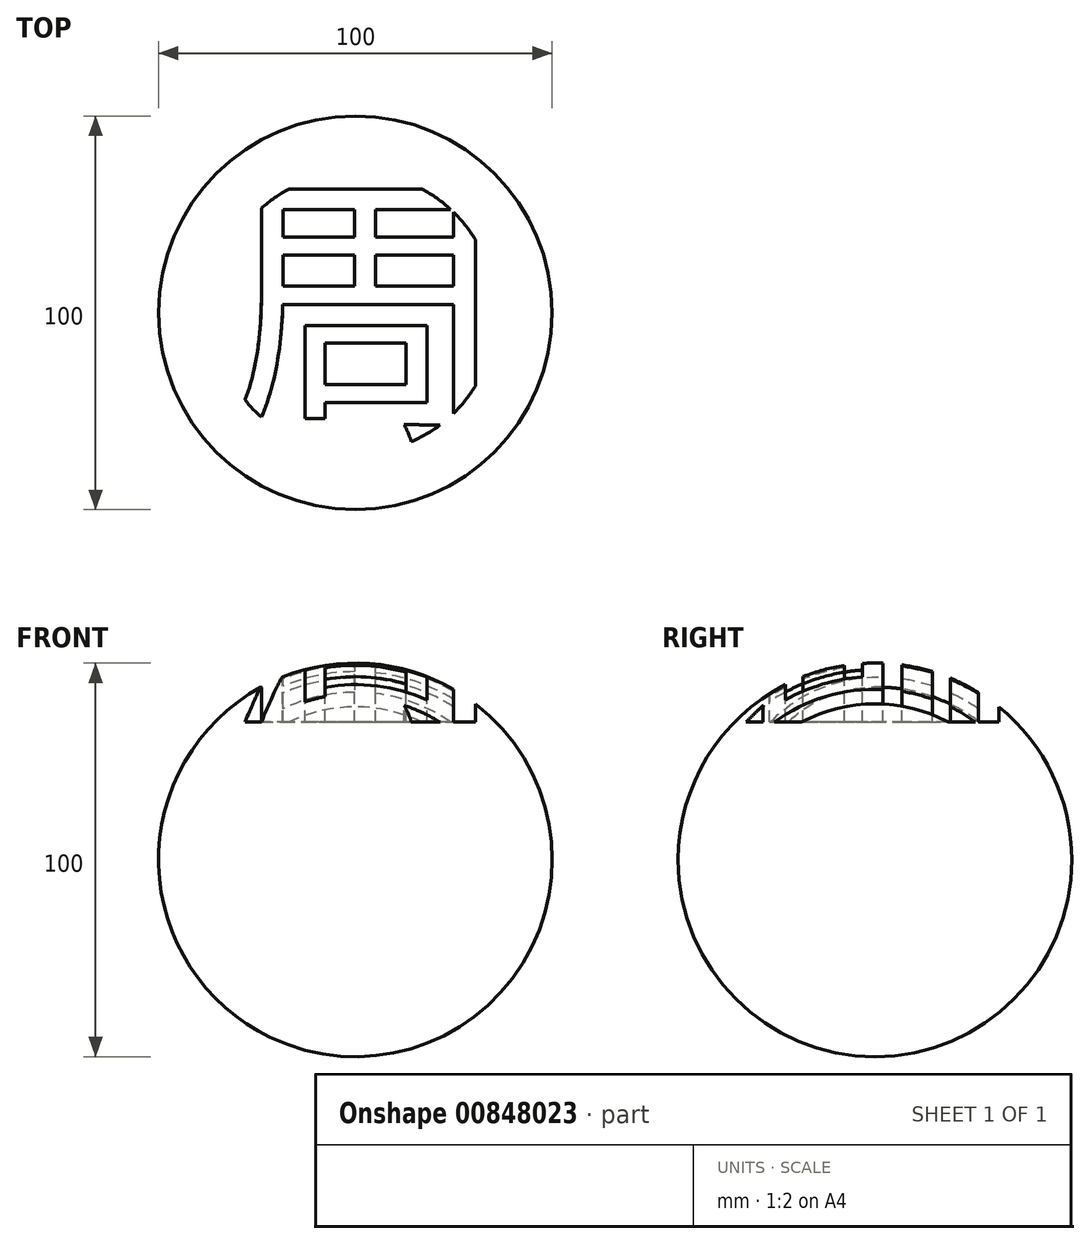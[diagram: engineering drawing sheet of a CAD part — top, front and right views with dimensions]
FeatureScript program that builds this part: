
annotation { "Feature Type Name" : "Feature", "Feature Type Description" : "" }
export const myFeature = defineFeature(function(context is Context, id is Id, definition is map)
    precondition{}
    {
        {
            var Q0;
            Q0=qCreatedBy(makeId("Top.planeOp"),FACE);
            var sketch = newSketch(context, id + "F0", { "sketchPlane" : qUnion([Q0])});
            skCircle(sketch, "E0", {"center": v(0, 0) * mm, "radius": 50 * mm});
            skLineSegment(sketch, "E1", {"start": v(0, 59.72) * mm, "end": v(0, -65.29) * mm});
            skSolve(sketch);
        }
        {
            var Q0;
            {var subQ0=sQuery(id+"F0.wireOp",EDGE,"E1");var subQ1=sQuery(id+"F0.wireOp",EDGE,"E0");var subQ2=makeQuery(id+"F0.imprint","INTERSECT",VERTEX,{"disambiguationData":[OD(0.0)],"derivedFrom":[subQ1,subQ0]});Q0=makeQuery(id+"F0.imprint","IMPRINT",FACE,{"disambiguationData":[TD([[makeQuery(id+"F0.imprint","IMPRINT",EDGE,{"disambiguationData":[TD([[subQ2,1.0]])],"derivedFrom":subQ1}),1.0]])]});}
            var Q1;
            Q1=sQuery(id+"F0.wireOp",EDGE,"E1");
            revolve(context, id + "F1", {"surfaceOperationType" : NewSurfaceOperationType.NEW, "entities" : qUnion([Q0]), "axis" : qUnion([Q1]), "revolveType" : RevolveType.FULL});
        }
        {
            var Q0;
            Q0=qCreatedBy(makeId("Top.planeOp"),FACE);
            cPlane(context, id + "F2", {"entities" : qUnion([Q0]), "cplaneType" : CPlaneType.OFFSET, "offset" : 50 * mm, "width" : 150 * mm, "height" : 150 * mm});
        }
        {
            var Q0;
            Q0=qCreatedBy(id+"F2.planeOp",FACE);
            var sketch = newSketch(context, id + "F3", { "sketchPlane" : qUnion([Q0])});
            skText(sketch, "E2", { "text": "周", "fontName": "NotoSansCJKtc-Regular.otf"});
            const initialGuessF3  = {"E2": [-0.03512, -0.02754, 1, 0, 0.05384]};
            skSetInitialGuess(sketch, initialGuessF3);
            skSolve(sketch);
        }
        {
            var Q0;
            Q0 = qSketchRegion(id + "F3", true);
            extrude(context, id + "F4", {"entities" : qUnion([Q0]), "operationType" : NewBodyOperationType.REMOVE, "oppositeDirection" : true, "depth" : 15 * mm, "offsetDistance" : 25 * mm});
        }
    });
